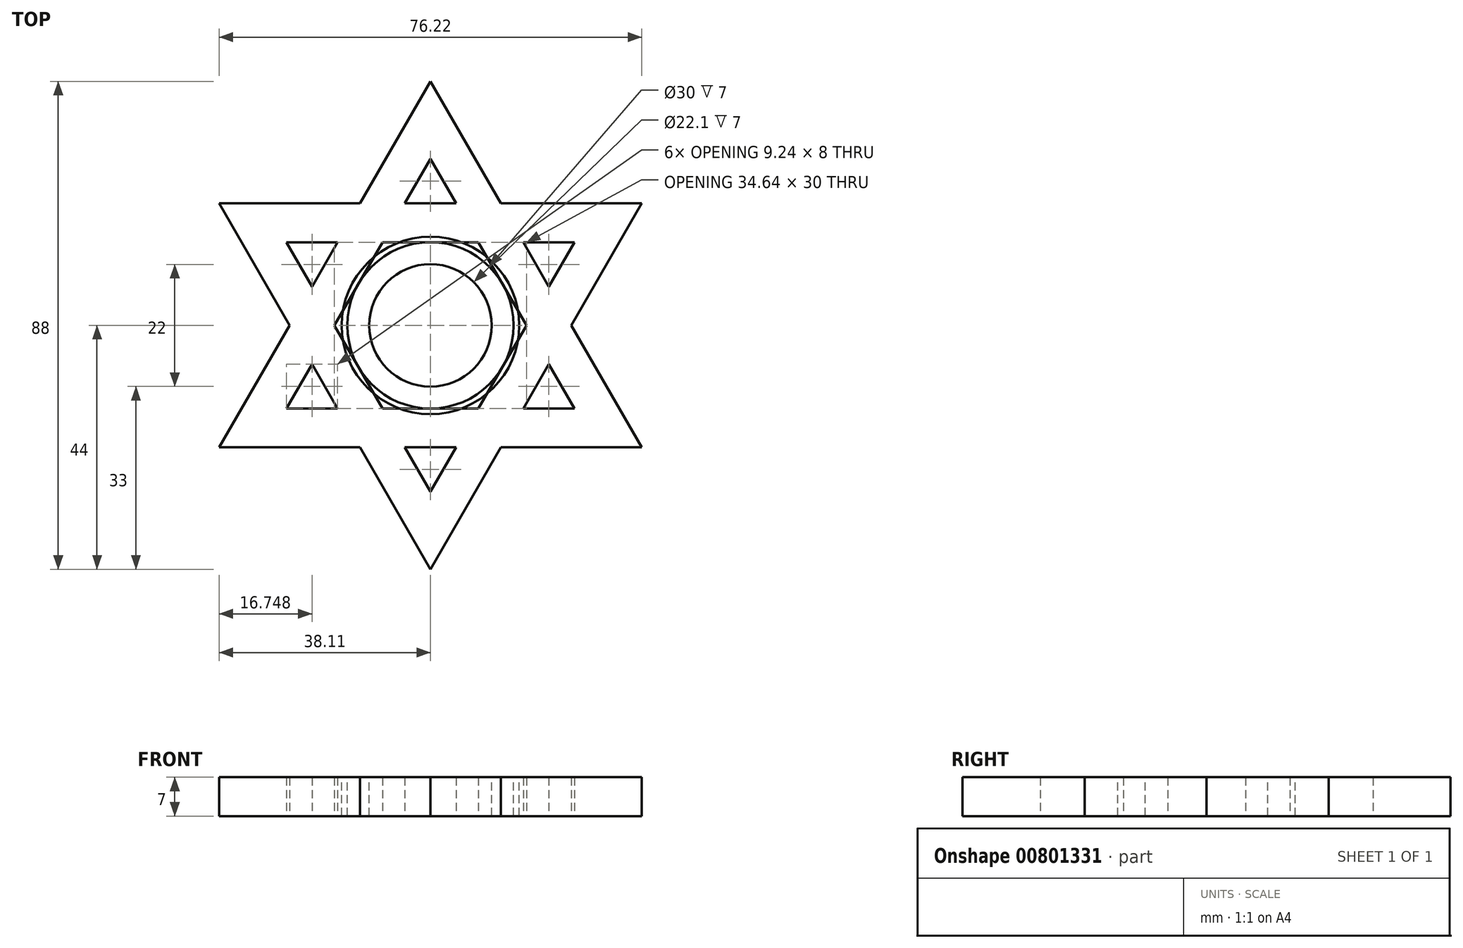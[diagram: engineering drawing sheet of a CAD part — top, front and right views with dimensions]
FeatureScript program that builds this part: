
annotation { "Feature Type Name" : "Feature", "Feature Type Description" : "" }
export const myFeature = defineFeature(function(context is Context, id is Id, definition is map)
    precondition{}
    {
        {
            var Q0;
            Q0=qCreatedBy(makeId("Top.planeOp"),FACE);
            var sketch = newSketch(context, id + "F0", { "sketchPlane" : qUnion([Q0])});
            skCircle(sketch, "E0", {"center": v(0, 0) * mm, "radius": 15 * mm});
            skLineSegment(sketch, "E1", {"start": v(-25.98, 15) * mm, "end": v(25.98, 15) * mm});
            skLineSegment(sketch, "E2", {"start": v(25.98, 15) * mm, "end": v(0, -30) * mm});
            skLineSegment(sketch, "E3", {"start": v(0, -30) * mm, "end": v(-25.98, 15) * mm});
            skLineSegment(sketch, "E4.0", {"start": v(-38.1, 22) * mm, "end": v(38.1, 22) * mm});
            skLineSegment(sketch, "E4.1", {"start": v(0, -44) * mm, "end": v(-38.1, 22) * mm});
            skLineSegment(sketch, "E4.2", {"start": v(38.1, 22) * mm, "end": v(0, -44) * mm});
            skLineSegment(sketch, "E5.1.0", {"start": v(38.1, -22) * mm, "end": v(-38.1, -22) * mm});
            skLineSegment(sketch, "E5.1.1", {"start": v(0, 44) * mm, "end": v(38.1, -22) * mm});
            skLineSegment(sketch, "E5.1.2", {"start": v(-38.1, -22) * mm, "end": v(0, 44) * mm});
            skLineSegment(sketch, "E6.0", {"start": v(-25.98, -15) * mm, "end": v(0, 30) * mm});
            skLineSegment(sketch, "E6.1", {"start": v(25.98, -15) * mm, "end": v(-25.98, -15) * mm});
            skLineSegment(sketch, "E6.2", {"start": v(0, 30) * mm, "end": v(25.98, -15) * mm});
            skSolve(sketch);
        }
        {
            var Q0;
            {var subQ6=sQuery(id+"F0.wireOp",EDGE,"E3");var subQ7=sQuery(id+"F0.wireOp",EDGE,"E1");var subQ8=makeQuery(id+"F0.imprint","INTERSECT",VERTEX,{"derivedFrom":[subQ7,subQ6]});Q0=makeQuery(id+"F0.imprint","IMPRINT",FACE,{"disambiguationData":[TD([[makeQuery(id+"F0.imprint","IMPRINT",EDGE,{"disambiguationData":[TD([[subQ8,-1.0]])],"derivedFrom":subQ7}),1.0]])]});}
            var Q1;
            {var subQ1=sQuery(id+"F0.wireOp",EDGE,"E5.1.0");var subQ3=sQuery(id+"F0.wireOp",EDGE,"E4.1");var subQ5=makeQuery(id+"F0.imprint","INTERSECT",VERTEX,{"derivedFrom":[subQ3,subQ1]});Q1=makeQuery(id+"F0.imprint","IMPRINT",FACE,{"disambiguationData":[TD([[makeQuery(id+"F0.imprint","IMPRINT",EDGE,{"disambiguationData":[TD([[subQ5,-1.0]])],"derivedFrom":subQ3}),1.0]])]});}
            var Q2;
            {var subQ5=sQuery(id+"F0.wireOp",EDGE,"E3");var subQ6=sQuery(id+"F0.wireOp",EDGE,"E2");var subQ7=makeQuery(id+"F0.imprint","INTERSECT",VERTEX,{"derivedFrom":[subQ6,subQ5]});Q2=makeQuery(id+"F0.imprint","IMPRINT",FACE,{"disambiguationData":[TD([[makeQuery(id+"F0.imprint","IMPRINT",EDGE,{"disambiguationData":[TD([[subQ7,1.0]])],"derivedFrom":subQ6}),1.0]])]});}
            var Q3;
            {var subQ0=sQuery(id+"F0.wireOp",EDGE,"E5.1.2");var subQ1=sQuery(id+"F0.wireOp",EDGE,"E1");var subQ2=makeQuery(id+"F0.imprint","INTERSECT",VERTEX,{"derivedFrom":[subQ1,subQ0]});Q3=makeQuery(id+"F0.imprint","IMPRINT",FACE,{"disambiguationData":[TD([[makeQuery(id+"F0.imprint","IMPRINT",EDGE,{"disambiguationData":[TD([[subQ2,-1.0]])],"derivedFrom":subQ1}),1.0]])]});}
            var Q4;
            {var subQ5=sQuery(id+"F0.wireOp",EDGE,"E1");var subQ6=makeQuery(id+"F0.imprint","INTERSECT",VERTEX,{"derivedFrom":[sQuery(id+"F0.wireOp",EDGE,"E0"),subQ5]});Q4=makeQuery(id+"F0.imprint","IMPRINT",FACE,{"disambiguationData":[TD([[makeQuery(id+"F0.imprint","IMPRINT",EDGE,{"disambiguationData":[TD([[subQ6,1.0]])],"derivedFrom":subQ5}),1.0]])]});}
            var Q5;
            {var subQ0=sQuery(id+"F0.wireOp",EDGE,"E6.2");var subQ1=sQuery(id+"F0.wireOp",EDGE,"E1");var subQ2=makeQuery(id+"F0.imprint","INTERSECT",VERTEX,{"derivedFrom":[subQ1,subQ0]});Q5=makeQuery(id+"F0.imprint","IMPRINT",FACE,{"disambiguationData":[TD([[makeQuery(id+"F0.imprint","IMPRINT",EDGE,{"disambiguationData":[TD([[subQ2,-1.0]])],"derivedFrom":subQ1}),1.0]])]});}
            var Q6;
            {var subQ5=sQuery(id+"F0.wireOp",EDGE,"E2");var subQ6=sQuery(id+"F0.wireOp",EDGE,"E1");var subQ7=makeQuery(id+"F0.imprint","INTERSECT",VERTEX,{"derivedFrom":[subQ6,subQ5]});Q6=makeQuery(id+"F0.imprint","IMPRINT",FACE,{"disambiguationData":[TD([[makeQuery(id+"F0.imprint","IMPRINT",EDGE,{"disambiguationData":[TD([[subQ7,1.0]])],"derivedFrom":subQ6}),1.0]])]});}
            var Q7;
            {var subQ0=sQuery(id+"F0.wireOp",EDGE,"E5.1.1");var subQ1=sQuery(id+"F0.wireOp",EDGE,"E2");var subQ2=makeQuery(id+"F0.imprint","INTERSECT",VERTEX,{"derivedFrom":[subQ1,subQ0]});Q7=makeQuery(id+"F0.imprint","IMPRINT",FACE,{"disambiguationData":[TD([[makeQuery(id+"F0.imprint","IMPRINT",EDGE,{"disambiguationData":[TD([[subQ2,-1.0]])],"derivedFrom":subQ1}),1.0]])]});}
            var Q8;
            {var subQ0=sQuery(id+"F0.wireOp",EDGE,"E5.1.1");var subQ3=sQuery(id+"F0.wireOp",EDGE,"E4.2");var subQ4=makeQuery(id+"F0.imprint","INTERSECT",VERTEX,{"derivedFrom":[subQ3,subQ0]});Q8=makeQuery(id+"F0.imprint","IMPRINT",FACE,{"disambiguationData":[TD([[makeQuery(id+"F0.imprint","IMPRINT",EDGE,{"disambiguationData":[TD([[subQ4,-1.0]])],"derivedFrom":subQ3}),1.0]])]});}
            var Q9;
            {var subQ0=sQuery(id+"F0.wireOp",EDGE,"E6.1");var subQ1=sQuery(id+"F0.wireOp",EDGE,"E2");var subQ2=makeQuery(id+"F0.imprint","INTERSECT",VERTEX,{"derivedFrom":[subQ1,subQ0]});Q9=makeQuery(id+"F0.imprint","IMPRINT",FACE,{"disambiguationData":[TD([[makeQuery(id+"F0.imprint","IMPRINT",EDGE,{"disambiguationData":[TD([[subQ2,-1.0]])],"derivedFrom":subQ1}),1.0]])]});}
            var Q10;
            {var subQ1=sQuery(id+"F0.wireOp",EDGE,"E2");var subQ7=makeQuery(id+"F0.imprint","INTERSECT",VERTEX,{"derivedFrom":[sQuery(id+"F0.wireOp",EDGE,"E0"),subQ1]});Q10=makeQuery(id+"F0.imprint","IMPRINT",FACE,{"disambiguationData":[TD([[makeQuery(id+"F0.imprint","IMPRINT",EDGE,{"disambiguationData":[TD([[subQ7,1.0]])],"derivedFrom":subQ1}),1.0]])]});}
            var Q11;
            {var subQ0=sQuery(id+"F0.wireOp",EDGE,"E5.1.0");var subQ1=sQuery(id+"F0.wireOp",EDGE,"E3");var subQ2=makeQuery(id+"F0.imprint","INTERSECT",VERTEX,{"derivedFrom":[subQ1,subQ0]});Q11=makeQuery(id+"F0.imprint","IMPRINT",FACE,{"disambiguationData":[TD([[makeQuery(id+"F0.imprint","IMPRINT",EDGE,{"disambiguationData":[TD([[subQ2,-1.0]])],"derivedFrom":subQ1}),1.0]])]});}
            var Q12;
            {var subQ5=sQuery(id+"F0.wireOp",EDGE,"E3");var subQ6=makeQuery(id+"F0.imprint","INTERSECT",VERTEX,{"derivedFrom":[sQuery(id+"F0.wireOp",EDGE,"E0"),subQ5]});Q12=makeQuery(id+"F0.imprint","IMPRINT",FACE,{"disambiguationData":[TD([[makeQuery(id+"F0.imprint","IMPRINT",EDGE,{"disambiguationData":[TD([[subQ6,1.0]])],"derivedFrom":subQ5}),1.0]])]});}
            var Q13;
            {var subQ0=sQuery(id+"F0.wireOp",EDGE,"E6.0");var subQ1=sQuery(id+"F0.wireOp",EDGE,"E3");var subQ2=makeQuery(id+"F0.imprint","INTERSECT",VERTEX,{"derivedFrom":[subQ1,subQ0]});Q13=makeQuery(id+"F0.imprint","IMPRINT",FACE,{"disambiguationData":[TD([[makeQuery(id+"F0.imprint","IMPRINT",EDGE,{"disambiguationData":[TD([[subQ2,-1.0]])],"derivedFrom":subQ1}),1.0]])]});}
            var Q14;
            {var subQ4=sQuery(id+"F0.wireOp",EDGE,"E5.1.2");var subQ5=sQuery(id+"F0.wireOp",EDGE,"E1");var subQ6=makeQuery(id+"F0.imprint","INTERSECT",VERTEX,{"derivedFrom":[subQ5,subQ4]});Q14=makeQuery(id+"F0.imprint","IMPRINT",FACE,{"disambiguationData":[TD([[makeQuery(id+"F0.imprint","IMPRINT",EDGE,{"disambiguationData":[TD([[subQ6,-1.0]])],"derivedFrom":subQ5}),-1.0]])]});}
            var Q15;
            {var subQ1=sQuery(id+"F0.wireOp",EDGE,"E1");var subQ5=sQuery(id+"F0.wireOp",EDGE,"E6.2");var subQ7=makeQuery(id+"F0.imprint","INTERSECT",VERTEX,{"derivedFrom":[subQ1,subQ5]});Q15=makeQuery(id+"F0.imprint","IMPRINT",FACE,{"disambiguationData":[TD([[makeQuery(id+"F0.imprint","IMPRINT",EDGE,{"disambiguationData":[TD([[subQ7,-1.0]])],"derivedFrom":subQ1}),-1.0]])]});}
            var Q16;
            {var subQ0=sQuery(id+"F0.wireOp",EDGE,"E5.1.2");var subQ3=sQuery(id+"F0.wireOp",EDGE,"E4.0");var subQ4=makeQuery(id+"F0.imprint","INTERSECT",VERTEX,{"derivedFrom":[subQ3,subQ0]});Q16=makeQuery(id+"F0.imprint","IMPRINT",FACE,{"disambiguationData":[TD([[makeQuery(id+"F0.imprint","IMPRINT",EDGE,{"disambiguationData":[TD([[subQ4,-1.0]])],"derivedFrom":subQ3}),1.0]])]});}
            var Q17;
            {var subQ0=sQuery(id+"F0.wireOp",EDGE,"E6.1");var subQ2=sQuery(id+"F0.wireOp",EDGE,"E2");var subQ3=makeQuery(id+"F0.imprint","INTERSECT",VERTEX,{"derivedFrom":[subQ2,subQ0]});Q17=makeQuery(id+"F0.imprint","IMPRINT",FACE,{"disambiguationData":[TD([[makeQuery(id+"F0.imprint","IMPRINT",EDGE,{"disambiguationData":[TD([[subQ3,-1.0]])],"derivedFrom":subQ2}),-1.0]])]});}
            var Q18;
            {var subQ0=sQuery(id+"F0.wireOp",EDGE,"E0");var subQ4=makeQuery(id+"F0.imprint","INTERSECT",VERTEX,{"derivedFrom":[subQ0,sQuery(id+"F0.wireOp",EDGE,"E1")]});Q18=makeQuery(id+"F0.imprint","IMPRINT",FACE,{"disambiguationData":[TD([[makeQuery(id+"F0.imprint","IMPRINT",EDGE,{"disambiguationData":[TD([[subQ4,1.0]])],"derivedFrom":subQ0}),1.0]])]});}
            extrude(context, id + "F1", {"entities" : qUnion([Q0, Q1, Q2, Q3, Q4, Q5, Q6, Q7, Q8, Q9, Q10, Q11, Q12, Q13, Q14, Q15, Q16, Q17, Q18]), "depth" : 7 * mm, "offsetDistance" : 25 * mm});
        }
        {
            var Q0;
            Q0=makeQuery(id+"F1.opExtrude","CAP_FACE",FACE,{"disambiguationData":[OSD([sQuery(id+"F0.wireOp",EDGE,"E0")])],"isStart":false});
            var sketch = newSketch(context, id + "F2", { "sketchPlane" : qUnion([Q0])});
            skCircle(sketch, "E7", {"center": v(0, 0) * mm, "radius": 16 * mm});
            skCircle(sketch, "E8", {"center": v(0, 0) * mm, "radius": 11.05 * mm});
            skSolve(sketch);
        }
        {
            var Q0;
            Q0=makeQuery(id+"F2.imprint","IMPRINT",FACE,{"disambiguationData":[TD([[makeQuery(id+"F2.imprint","IMPRINT",EDGE,{"derivedFrom":sQuery(id+"F2.wireOp",EDGE,"E7")}),1.0]])]});
            extrude(context, id + "F3", {"entities" : qUnion([Q0]), "oppositeDirection" : true, "depth" : 7 * mm, "offsetDistance" : 25 * mm});
        }
        {
            var Q0;
            Q0=makeQuery(id+"F2.imprint","IMPRINT",FACE,{"disambiguationData":[TD([[makeQuery(id+"F2.imprint","IMPRINT",EDGE,{"derivedFrom":sQuery(id+"F2.wireOp",EDGE,"E8")}),1.0]])]});
            extrude(context, id + "F4", {"entities" : qUnion([Q0]), "operationType" : NewBodyOperationType.REMOVE, "endBound" : BoundingType.THROUGH_ALL, "oppositeDirection" : true, "depth" : 25 * mm, "offsetDistance" : 25 * mm});
        }
    });
